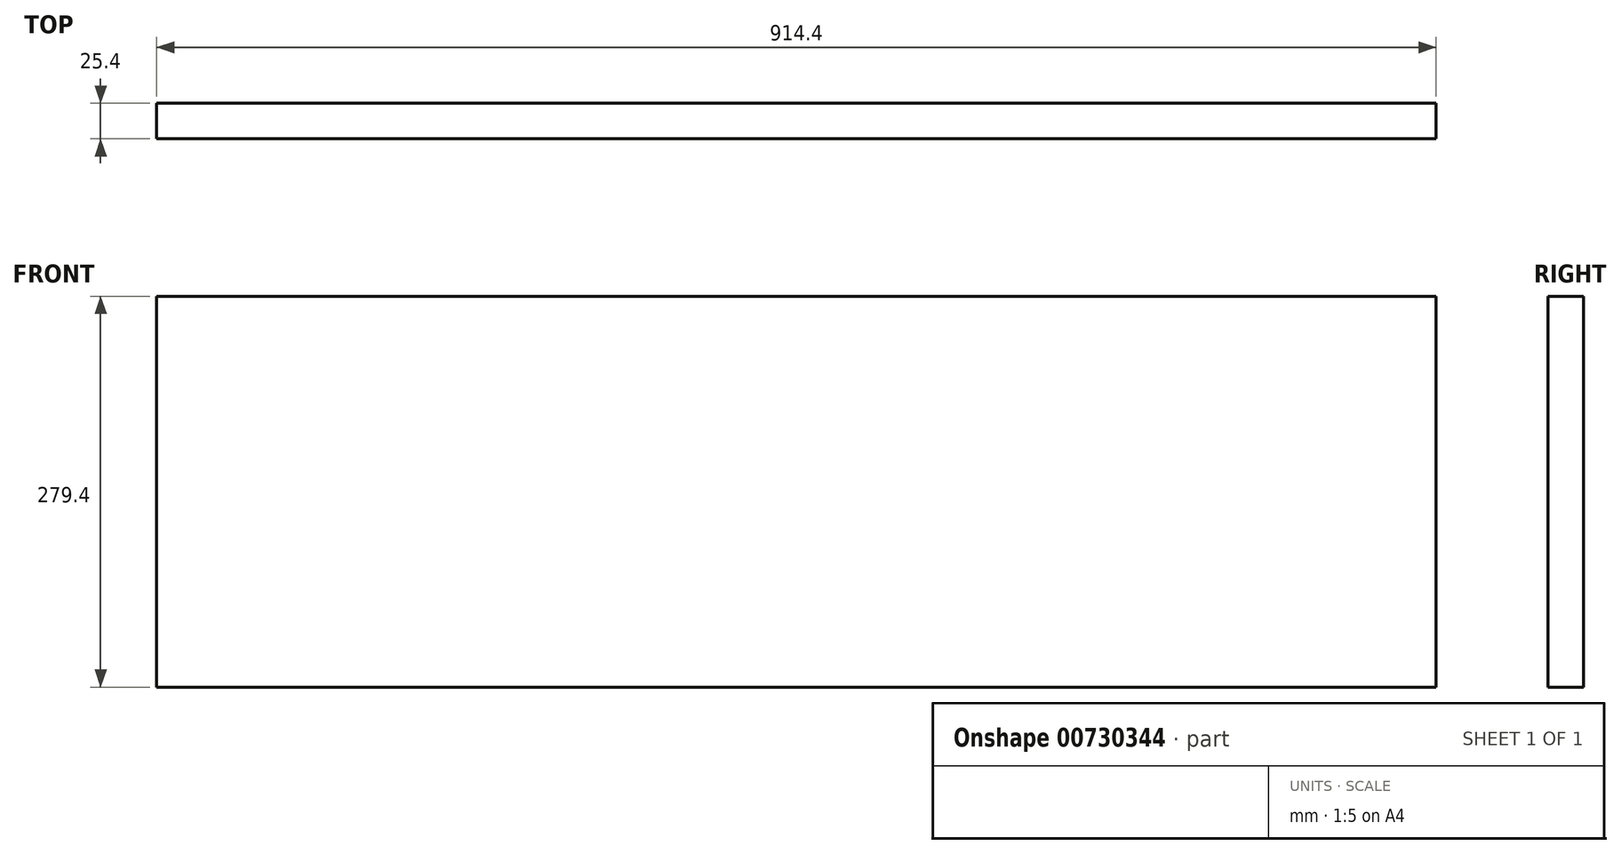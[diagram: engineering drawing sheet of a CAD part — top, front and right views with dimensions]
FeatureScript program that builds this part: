
annotation { "Feature Type Name" : "Feature", "Feature Type Description" : "" }
export const myFeature = defineFeature(function(context is Context, id is Id, definition is map)
    precondition{}
    {
        {
            var Q0;
            Q0=qCreatedBy(makeId("Top.planeOp"),FACE);
            var sketch = newSketch(context, id + "F0", { "sketchPlane" : qUnion([Q0])});
            skLineSegment(sketch, "E0.bottom", {"start": v(457.2, -12.7) * mm, "end": v(-457.2, -12.7) * mm});
            skLineSegment(sketch, "E0.top", {"start": v(457.2, 12.7) * mm, "end": v(-457.2, 12.7) * mm});
            skLineSegment(sketch, "E0.left", {"start": v(457.2, -12.7) * mm, "end": v(457.2, 12.7) * mm});
            skLineSegment(sketch, "E0.right", {"start": v(-457.2, -12.7) * mm, "end": v(-457.2, 12.7) * mm});
            skPoint(sketch, "E0.middle", {"position": v(0, 0) * mm});
            skSolve(sketch);
        }
        {
            var Q0;
            Q0=makeQuery(id+"F0.imprint","IMPRINT",FACE,{"disambiguationData":[TD([[makeQuery(id+"F0.imprint","IMPRINT",EDGE,{"derivedFrom":sQuery(id+"F0.wireOp",EDGE,"E0.bottom")}),-1.0]])]});
            extrude(context, id + "F1", {"entities" : qUnion([Q0]), "endBound" : BoundingType.SYMMETRIC, "depth" : 279.4 * mm, "offsetDistance" : 25.4 * mm});
        }
    });
